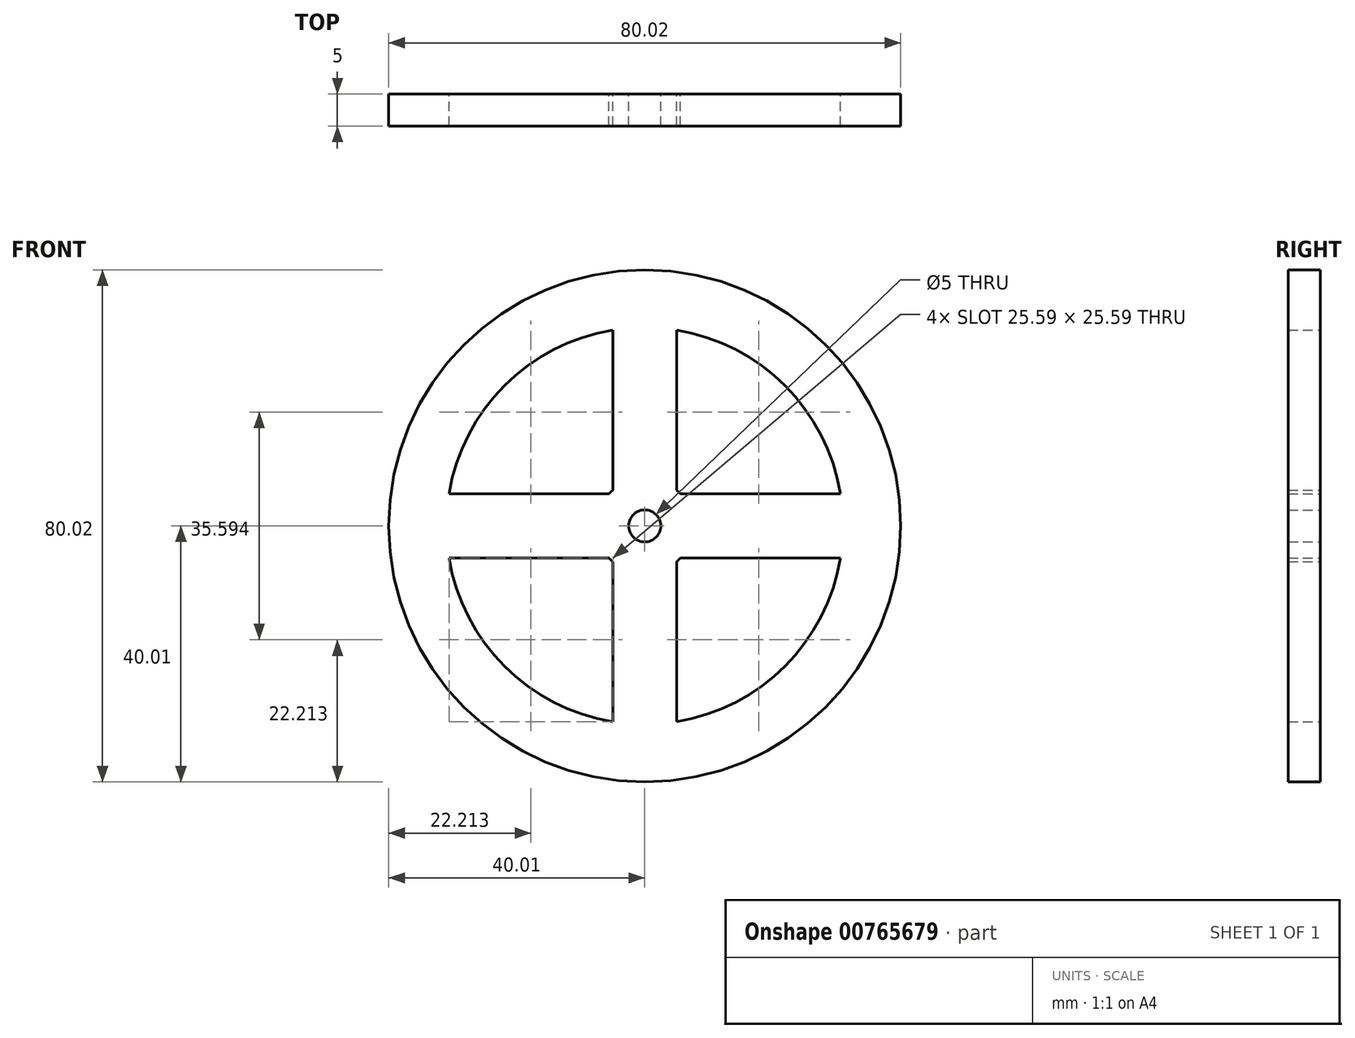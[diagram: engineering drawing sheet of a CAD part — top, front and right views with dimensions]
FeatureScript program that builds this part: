
annotation { "Feature Type Name" : "Feature", "Feature Type Description" : "" }
export const myFeature = defineFeature(function(context is Context, id is Id, definition is map)
    precondition{}
    {
        {
            var Q0;
            Q0=qCreatedBy(makeId("Front.planeOp"),FACE);
            var sketch = newSketch(context, id + "F0", { "sketchPlane" : qUnion([Q0])});
            skCircle(sketch, "E0", {"center": v(0, 0) * mm, "radius": 40 * mm});
            skArc(sketch, "E1", {"start": v(-30.6, -5) * mm, "mid": v(-21.92, -21.92) * mm, "end": v(-5, -30.6) * mm});
            skArc(sketch, "E2", {"start": v(5.6, 5) * mm, "mid": v(5.3, 5.3) * mm, "end": v(5, 5.6) * mm});
            skCircle(sketch, "E3", {"center": v(0, 0) * mm, "radius": 2.5 * mm});
            skLineSegment(sketch, "E4", {"start": v(0, 0) * mm, "end": v(0, 31) * mm, "construction": true});
            skLineSegment(sketch, "E5", {"start": v(0, 0) * mm, "end": v(31, 0) * mm, "construction": true});
            skLineSegment(sketch, "E6", {"start": v(0, 0) * mm, "end": v(0, -31) * mm, "construction": true});
            skLineSegment(sketch, "E7", {"start": v(0, 0) * mm, "end": v(-31, 0) * mm, "construction": true});
            skLineSegment(sketch, "E8.0", {"start": v(5, 5.6) * mm, "end": v(5, 30.6) * mm});
            skLineSegment(sketch, "E9.0", {"start": v(-5, 5.6) * mm, "end": v(-5, 30.6) * mm});
            skLineSegment(sketch, "E10.0", {"start": v(5.6, -5) * mm, "end": v(30.6, -5) * mm});
            skLineSegment(sketch, "E11.0", {"start": v(5.6, 5) * mm, "end": v(30.6, 5) * mm});
            skLineSegment(sketch, "E12.0", {"start": v(5, -5.6) * mm, "end": v(5, -30.6) * mm});
            skLineSegment(sketch, "E13.0", {"start": v(-5, -5.6) * mm, "end": v(-5, -30.6) * mm});
            skLineSegment(sketch, "E14.0", {"start": v(-5.6, 5) * mm, "end": v(-30.6, 5) * mm});
            skLineSegment(sketch, "E15.0", {"start": v(-5.6, -5) * mm, "end": v(-30.6, -5) * mm});
            skLineSegment(sketch, "E16.trimOffspring", {"start": v(-39.7, 5) * mm, "end": v(-40, 5) * mm});
            skLineSegment(sketch, "E17.trimOffspring", {"start": v(-39.7, -5) * mm, "end": v(-40, -5) * mm});
            skLineSegment(sketch, "E18.trimOffspring", {"start": v(-5, 39.7) * mm, "end": v(-5, 40) * mm});
            skLineSegment(sketch, "E19.trimOffspring", {"start": v(5, 39.7) * mm, "end": v(5, 40) * mm});
            skLineSegment(sketch, "E20.trimOffspring", {"start": v(39.7, -5) * mm, "end": v(40, -5) * mm});
            skLineSegment(sketch, "E21.trimOffspring", {"start": v(39.7, 5) * mm, "end": v(40, 5) * mm});
            skLineSegment(sketch, "E22.trimOffspring", {"start": v(5, -39.7) * mm, "end": v(5, -40) * mm});
            skLineSegment(sketch, "E23.trimOffspring", {"start": v(-5, -39.7) * mm, "end": v(-5, -40) * mm});
            skArc(sketch, "E24.trimOffspring", {"start": v(-5, 30.6) * mm, "mid": v(-21.92, 21.92) * mm, "end": v(-30.6, 5) * mm});
            skArc(sketch, "E25.trimOffspring", {"start": v(30.6, 5) * mm, "mid": v(21.92, 21.92) * mm, "end": v(5, 30.6) * mm});
            skArc(sketch, "E26.trimOffspring", {"start": v(5, -5.6) * mm, "mid": v(5.3, -5.3) * mm, "end": v(5.6, -5) * mm});
            skArc(sketch, "E27.trimOffspring", {"start": v(-5.6, -5) * mm, "mid": v(-5.3, -5.3) * mm, "end": v(-5, -5.6) * mm});
            skArc(sketch, "E28.trimOffspring", {"start": v(-5, 5.6) * mm, "mid": v(-5.3, 5.3) * mm, "end": v(-5.6, 5) * mm});
            skArc(sketch, "E29.trimOffspring", {"start": v(5, -30.6) * mm, "mid": v(21.92, -21.92) * mm, "end": v(30.6, -5) * mm});
            skSolve(sketch);
        }
        {
            var Q0;
            Q0 = qSketchRegion(id + "F0", true);
            extrude(context, id + "F1", {"entities" : qUnion([Q0]), "endBound" : BoundingType.SYMMETRIC, "depth" : 5 * mm, "offsetDistance" : 25.4 * mm});
        }
    });
